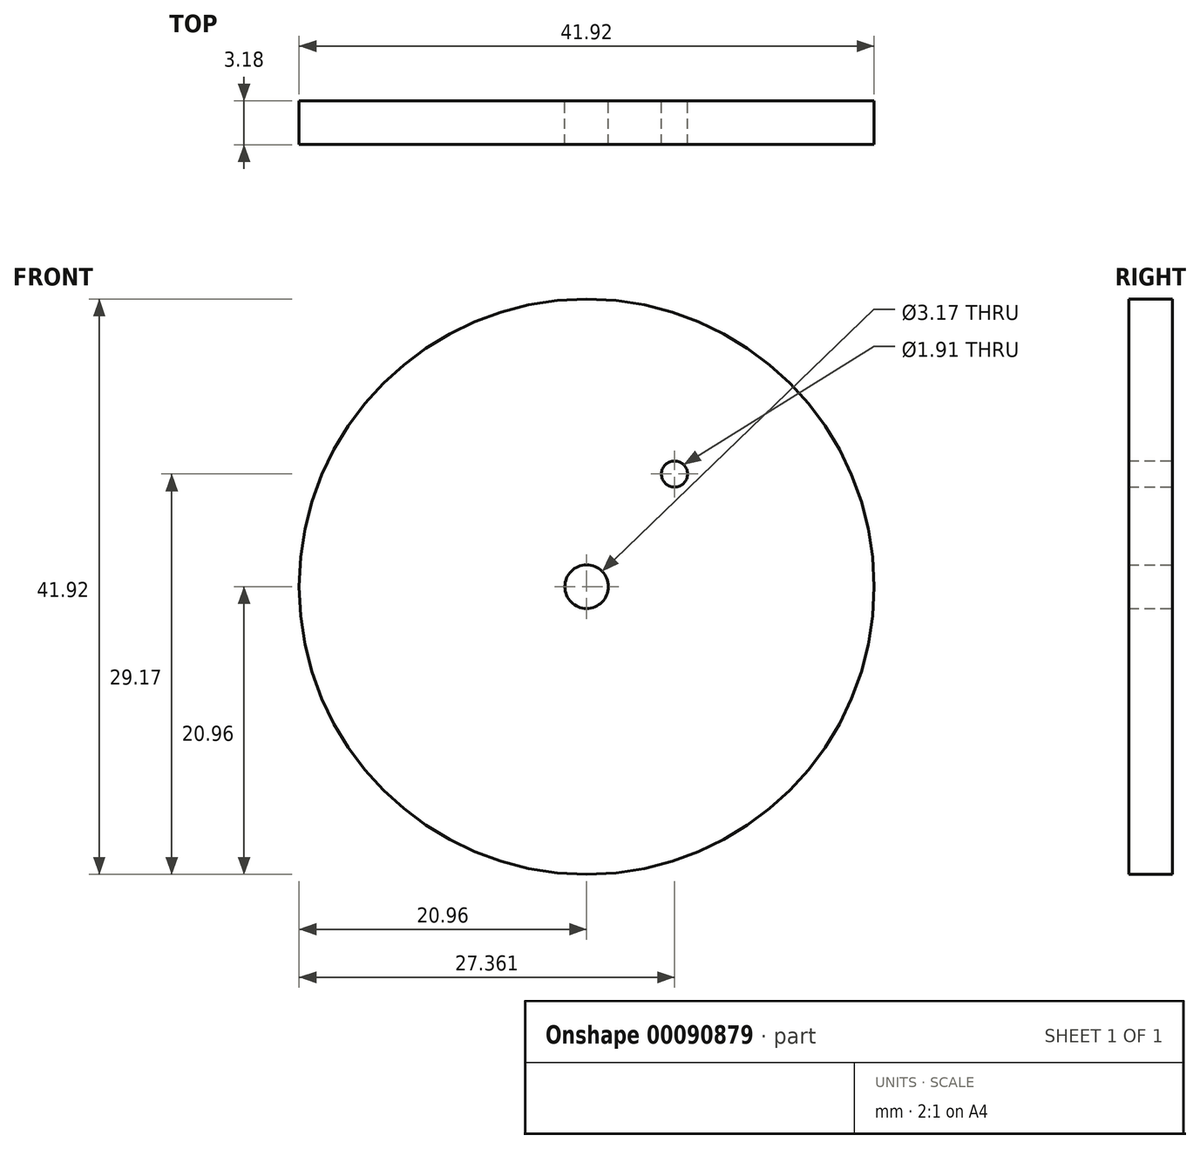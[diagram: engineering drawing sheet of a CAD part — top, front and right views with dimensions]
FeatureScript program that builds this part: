
annotation { "Feature Type Name" : "Feature", "Feature Type Description" : "" }
export const myFeature = defineFeature(function(context is Context, id is Id, definition is map)
    precondition{}
    {
        {
            var Q0;
            Q0=qCreatedBy(makeId("Front.planeOp"),FACE);
            var sketch = newSketch(context, id + "F0", { "sketchPlane" : qUnion([Q0])});
            skCircle(sketch, "E0", {"center": v(0, 0) * mm, "radius": 20.96 * mm});
            skCircle(sketch, "E1", {"center": v(0, 0) * mm, "radius": 1.59 * mm});
            skCircle(sketch, "E2", {"center": v(6.4, 8.2) * mm, "radius": 0.95 * mm});
            skSolve(sketch);
        }
        {
            var Q0;
            Q0 = qSketchRegion(id + "F0", true);
            extrude(context, id + "F1", {"entities" : qUnion([Q0]), "endBound" : BoundingType.SYMMETRIC, "depth" : 3.17 * mm});
        }
    });
